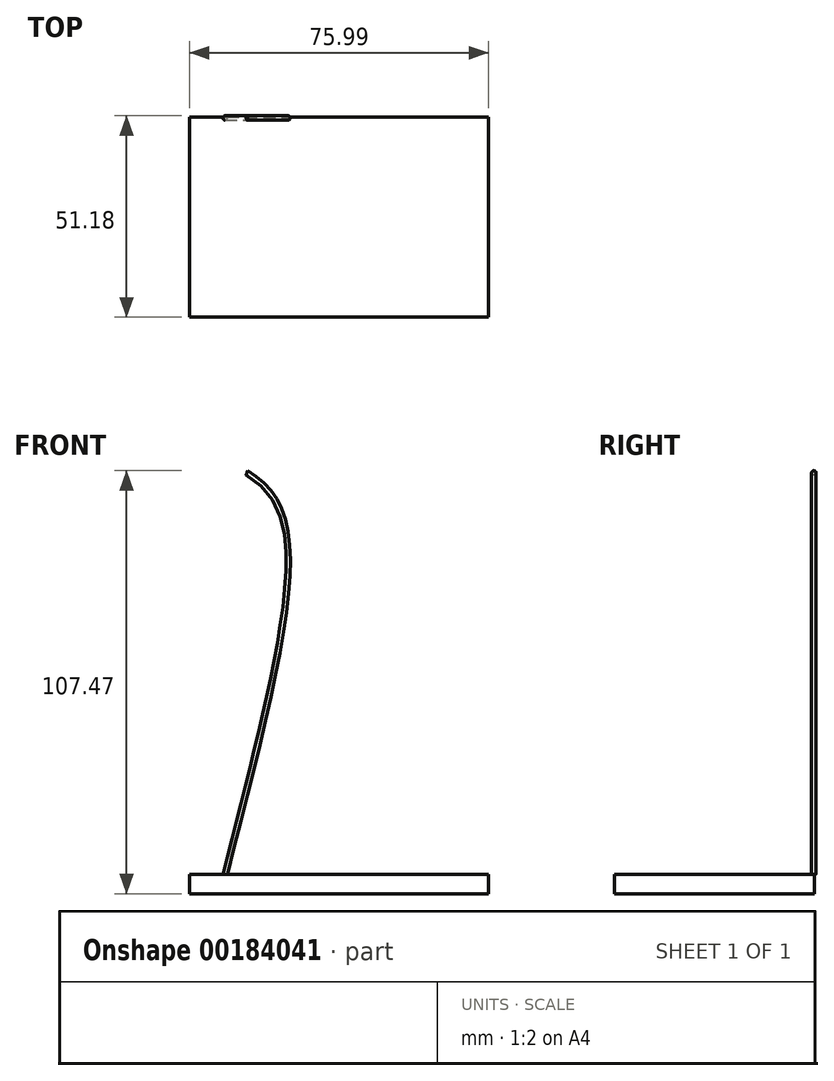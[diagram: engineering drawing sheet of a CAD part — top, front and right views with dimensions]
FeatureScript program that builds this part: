
annotation { "Feature Type Name" : "Feature", "Feature Type Description" : "" }
export const myFeature = defineFeature(function(context is Context, id is Id, definition is map)
    precondition{}
    {
        {
            var Q0;
            Q0=qCreatedBy(makeId("Front.planeOp"),FACE);
            var sketch = newSketch(context, id + "F0", { "sketchPlane" : qUnion([Q0])});
            skLineSegment(sketch, "E0.bottom", {"start": v(-31.25, -38.58) * mm, "end": v(44.74, -38.58) * mm});
            skLineSegment(sketch, "E0.top", {"start": v(-31.25, -43.56) * mm, "end": v(44.74, -43.56) * mm});
            skLineSegment(sketch, "E0.left", {"start": v(-31.25, -38.58) * mm, "end": v(-31.25, -43.56) * mm});
            skLineSegment(sketch, "E0.right", {"start": v(44.74, -38.58) * mm, "end": v(44.74, -43.56) * mm});
            skSolve(sketch);
        }
        {
            var Q0;
            Q0=qCreatedBy(makeId("Front.planeOp"),FACE);
            var sketch = newSketch(context, id + "F1", { "sketchPlane" : qUnion([Q0])});
            skFitSpline(sketch, "E1", {"points": [v(-22.18, -38.5) * mm, v(-6.56, 47.19) * mm, v(-16.76, 63.4) * mm], "startDerivative": vector(39.96, 157.42) * mm, "endDerivative": vector(-53, 31.2) * mm});
            skFitSpline(sketch, "E2", {"points": [v(29.28, -39.85) * mm, v(8.94, 48.57) * mm, v(20.5, 63.4) * mm], "startDerivative": vector(-68.73, 160.67) * mm, "endDerivative": vector(60.7, 32.03) * mm});
            skPoint(sketch, "E3", {"position": v(28.81, -38.75) * mm});
            skPoint(sketch, "E4", {"position": v(28.74, -38.58) * mm});
            skSolve(sketch);
        }
        {
            var Q0;
            Q0 = qSketchRegion(id + "F0", true);
            extrude(context, id + "F2", {"entities" : qUnion([Q0]), "depth" : 50.8 * mm});
        }
        {
            var Q0;
            Q0=makeQuery(id+"F2.opExtrude","SWEPT_FACE",FACE,{"disambiguationData":[OSD([sQuery(id+"F0.wireOp",EDGE,"E0.bottom")])]});
            var sketch = newSketch(context, id + "F3", { "sketchPlane" : qUnion([Q0])});
            skCircle(sketch, "E5", {"center": v(-22.17, -0.17) * mm, "radius": 0.55 * mm});
            skSolve(sketch);
        }
        {
            var Q0;
            {var subQ0=sQuery(id+"F3.wireOp",EDGE,"E5");var subQ1=makeQuery(id+"F2.opExtrude","CAP_EDGE",EDGE,{"disambiguationData":[OSD([sQuery(id+"F0.wireOp",EDGE,"E0.bottom")])],"isStart":true});var subQ2=makeQuery(id+"F3.imprint","INTERSECT",VERTEX,{"disambiguationData":[OD(0.0)],"derivedFrom":[subQ1,subQ0]});Q0=makeQuery(id+"F3.imprint","IMPRINT",FACE,{"disambiguationData":[TD([[makeQuery(id+"F3.imprint","IMPRINT",EDGE,{"disambiguationData":[TD([[subQ2,1.0]])],"derivedFrom":subQ0}),1.0]])]});}
            var Q1;
            {var subQ0=sQuery(id+"F3.wireOp",EDGE,"E5");var subQ1=makeQuery(id+"F2.opExtrude","CAP_EDGE",EDGE,{"disambiguationData":[OSD([sQuery(id+"F0.wireOp",EDGE,"E0.bottom")])],"isStart":true});var subQ2=makeQuery(id+"F3.imprint","INTERSECT",VERTEX,{"disambiguationData":[OD(0.0)],"derivedFrom":[subQ1,subQ0]});Q1=makeQuery(id+"F3.imprint","IMPRINT",FACE,{"disambiguationData":[TD([[makeQuery(id+"F3.imprint","IMPRINT",EDGE,{"disambiguationData":[TD([[subQ2,-1.0]])],"derivedFrom":subQ0}),1.0]])]});}
            var Q2;
            Q2=sQuery(id+"F1.wireOp",EDGE,"E1");
            sweep(context, id + "F4", {"operationType" : NewBodyOperationType.ADD, "profiles" : qUnion([Q0, Q1]), "path" : qUnion([Q2])});
        }
    });
